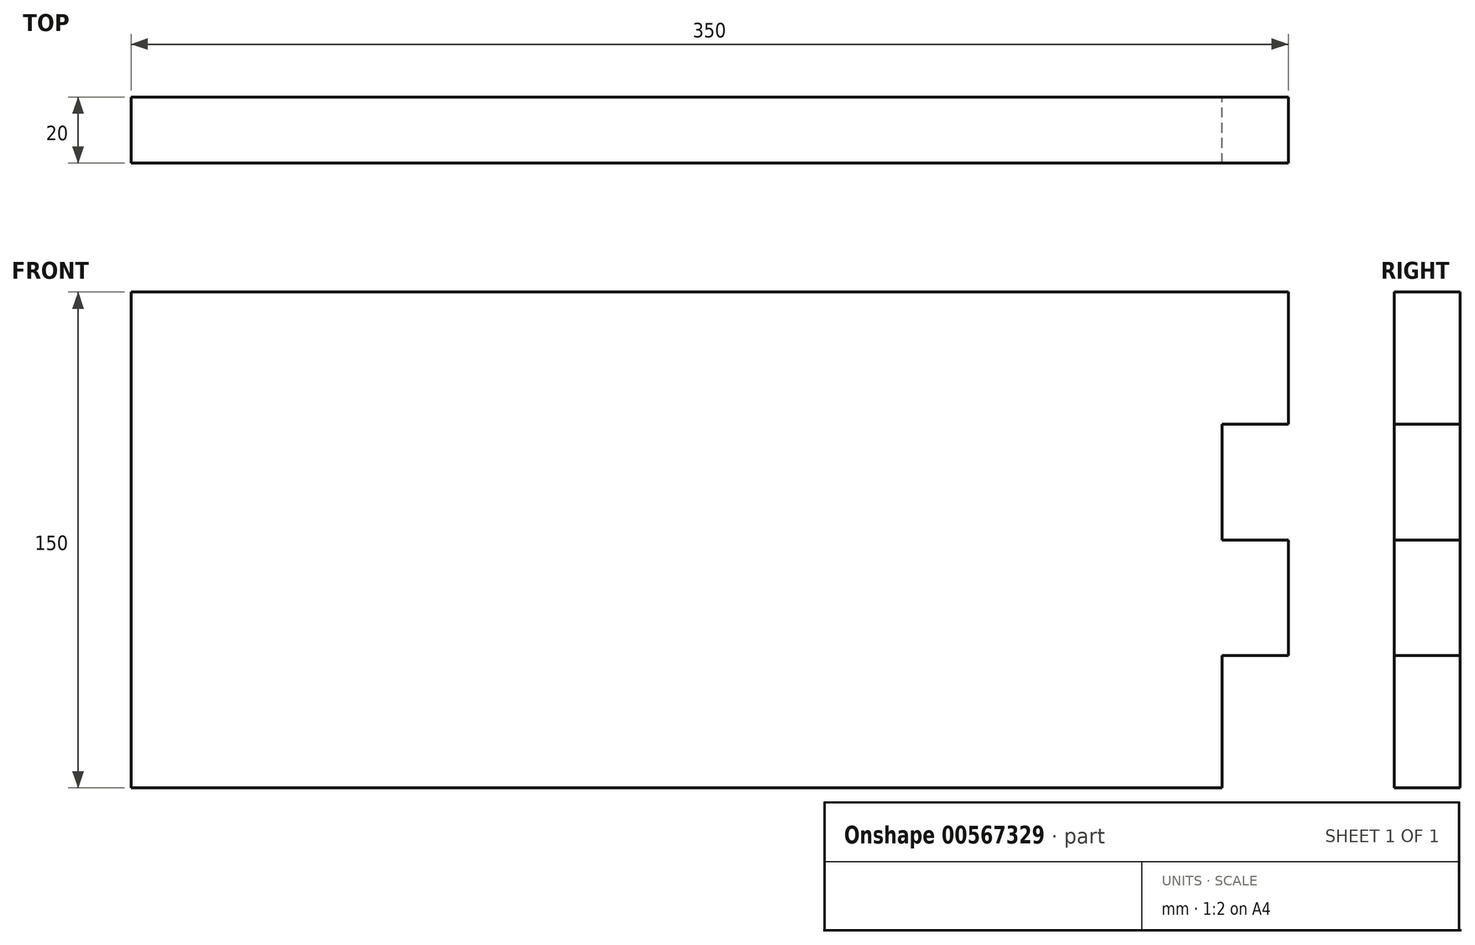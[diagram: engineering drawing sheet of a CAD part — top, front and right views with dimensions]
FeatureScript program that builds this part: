
annotation { "Feature Type Name" : "Feature", "Feature Type Description" : "" }
export const myFeature = defineFeature(function(context is Context, id is Id, definition is map)
    precondition{}
    {
        {
            var Q0;
            Q0=qCreatedBy(makeId("Front.planeOp"),FACE);
            var sketch = newSketch(context, id + "F0", { "sketchPlane" : qUnion([Q0])});
            skLineSegment(sketch, "E0.bottom", {"start": v(-20, 0) * mm, "end": v(-350, 0) * mm});
            skLineSegment(sketch, "E0.top", {"start": v(0, 150) * mm, "end": v(-350, 150) * mm});
            skLineSegment(sketch, "E0.left", {"start": v(0, 40) * mm, "end": v(0, 75) * mm});
            skLineSegment(sketch, "E0.right", {"start": v(-350, 0) * mm, "end": v(-350, 150) * mm});
            skLineSegment(sketch, "E1", {"start": v(-20, 110) * mm, "end": v(-20, 75) * mm});
            skLineSegment(sketch, "E2", {"start": v(-20, 75) * mm, "end": v(0, 75) * mm});
            skLineSegment(sketch, "E3", {"start": v(-20, 40) * mm, "end": v(0, 40) * mm});
            skLineSegment(sketch, "E4", {"start": v(-20, 110) * mm, "end": v(0, 110) * mm});
            skLineSegment(sketch, "E5.trimOffspring", {"start": v(0, 110) * mm, "end": v(0, 150) * mm});
            skPoint(sketch, "E6.orphan", {"position": v(0, 0) * mm});
            skLineSegment(sketch, "E7.trimOffspring", {"start": v(-20, 40) * mm, "end": v(-20, 0) * mm});
            skPoint(sketch, "E8.orphan", {"position": v(-20, 150) * mm});
            skSolve(sketch);
        }
        {
            var Q0;
            Q0=makeQuery(id+"F0.imprint","IMPRINT",FACE,{"disambiguationData":[TD([[makeQuery(id+"F0.imprint","IMPRINT",EDGE,{"derivedFrom":sQuery(id+"F0.wireOp",EDGE,"E0.bottom")}),-1.0]])]});
            extrude(context, id + "F1", {"entities" : qUnion([Q0]), "depth" : 20 * mm, "offsetDistance" : 25.4 * mm});
        }
        {
            var Q0;
            Q0=makeQuery(id+"F0.imprint","IMPRINT",FACE,{"disambiguationData":[TD([[makeQuery(id+"F0.imprint","IMPRINT",EDGE,{"derivedFrom":sQuery(id+"F0.wireOp",EDGE,"E0.bottom")}),-1.0]])]});
            extrude(context, id + "F2", {"entities" : qUnion([Q0]), "depth" : 20 * mm, "offsetDistance" : 25.4 * mm});
        }
    });
